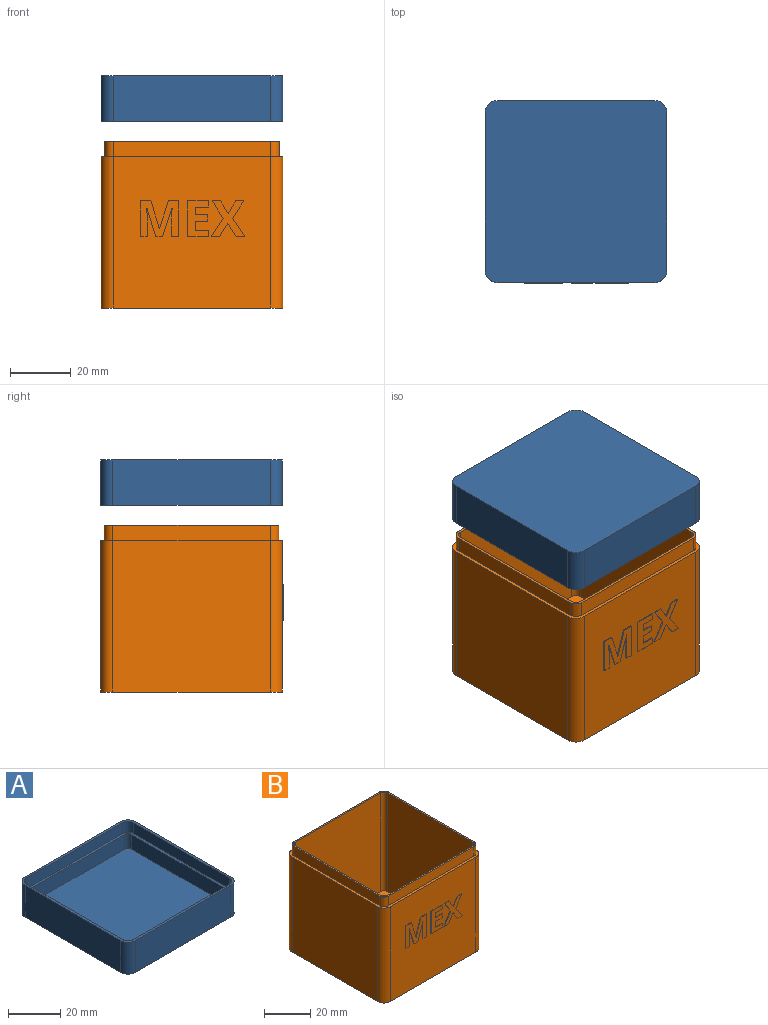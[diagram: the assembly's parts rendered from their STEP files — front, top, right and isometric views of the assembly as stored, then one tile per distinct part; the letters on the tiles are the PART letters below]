
ASSEMBLY  parts=2 mates=2
PART A: 28 faces, bbox 60x60x15 mm
  f0: plane 58x58mm, normal (0,0,1), area 223.7mm2, adj f11,f12,f13,f14,f15,f16,f17,f18
  f1: plane 60x60mm, normal (0,0,1), area 230mm2, adj f2,f3,f4,f5,f6,f7,f8,f9
  f2: plane 52x15mm, normal (0,1,0), area 780mm2, adj f1,f3,f9,f10
  f3: cylinder r=4mm len=15mm, axis (0,0,1), area 94.2mm2, adj f1,f2,f4,f10
  f4: plane 52x15mm, normal (-1,0,0), area 780mm2, adj f1,f3,f5,f10
  f5: cylinder r=4mm len=15mm, axis (0,0,1), area 94.2mm2, adj f1,f4,f6,f10
  f6: plane 52x15mm, normal (0,-1,0), area 780mm2, adj f1,f5,f7,f10
  f7: cylinder r=4mm len=15mm, axis (0,0,1), area 94.2mm2, adj f1,f6,f8,f10
  f8: plane 52x15mm, normal (1,0,0), area 780mm2, adj f1,f7,f9,f10
  f9: cylinder r=4mm len=15mm, axis (0,0,1), area 94.2mm2, adj f1,f2,f8,f10
  f10: plane 60x60mm, normal (0,0,-1), area 3586.3mm2, adj f2,f3,f4,f5,f6,f7,f8,f9
  f11: plane 52x5.1mm, normal (0,-1,0), area 265.2mm2, adj f0,f1,f12,f18
  f12: cylinder r=3mm len=5.1mm, axis (0,0,1), area 24mm2, adj f0,f1,f11,f13
  f13: plane 52x5.1mm, normal (1,0,0), area 265.2mm2, adj f0,f1,f12,f14
  f14: cylinder r=3mm len=5.1mm, axis (0,0,1), area 24mm2, adj f0,f1,f13,f15
  f15: plane 52x5.1mm, normal (0,1,0), area 265.2mm2, adj f0,f1,f14,f16
  f16: cylinder r=3mm len=5.1mm, axis (0,0,1), area 24mm2, adj f0,f1,f15,f17
  f17: plane 52x5.1mm, normal (-1,0,0), area 265.2mm2, adj f0,f1,f16,f18
  f18: cylinder r=3mm len=5.1mm, axis (0,0,1), area 24mm2, adj f0,f1,f11,f17
  f19: plane 52x6.9mm, normal (0,-1,0), area 358.8mm2, adj f0,f20,f26,f27
  f20: cylinder r=2mm len=6.9mm, axis (0,0,-1), area 21.7mm2, adj f0,f19,f21,f27
  f21: plane 52x6.9mm, normal (1,0,0), area 358.8mm2, adj f0,f20,f22,f27
  f22: cylinder r=2mm len=6.9mm, axis (0,0,-1), area 21.7mm2, adj f0,f21,f23,f27
  f23: plane 52x6.9mm, normal (0,1,0), area 358.8mm2, adj f0,f22,f24,f27
  f24: cylinder r=2mm len=6.9mm, axis (0,0,-1), area 21.7mm2, adj f0,f23,f25,f27
  f25: plane 52x6.9mm, normal (-1,0,0), area 358.8mm2, adj f0,f24,f26,f27
  f26: cylinder r=2mm len=6.9mm, axis (0,0,-1), area 21.7mm2, adj f0,f19,f25,f27
  f27: plane 56x56mm, normal (0,0,1), area 3132.6mm2, adj f19,f20,f21,f22,f23,f24,f25,f26
PART B: 74 faces, bbox 60x60.3x55 mm
  f0: plane 52x50mm, normal (0,-1,0), area 2389.2mm2, adj f2,f8,f9,f10,f28,f29,f30,f31
  f1: plane 57.6x57.6mm, normal (0,0,1), area 178.5mm2, adj f11,f12,f13,f14,f15,f16,f17,f18
  f2: plane 60x60mm, normal (0,0,1), area 275.2mm2, adj f0,f3,f4,f5,f6,f7,f8,f9
  f3: plane 52x50mm, normal (1,0,0), area 2600mm2, adj f2,f4,f9,f10
  f4: cylinder r=4mm len=50mm, axis (0,0,1), area 314.2mm2, adj f2,f3,f5,f10
  f5: plane 52x50mm, normal (0,1,0), area 2600mm2, adj f2,f4,f6,f10
  f6: cylinder r=4mm len=50mm, axis (0,0,1), area 314.2mm2, adj f2,f5,f7,f10
  f7: plane 52x50mm, normal (-1,0,0), area 2600mm2, adj f2,f6,f8,f10
  f8: cylinder r=4mm len=50mm, axis (0,0,1), area 314.2mm2, adj f0,f2,f7,f10
  f9: cylinder r=4mm len=50mm, axis (0,0,1), area 314.2mm2, adj f0,f2,f3,f10
  f10: plane 60x60mm, normal (0,0,-1), area 3586.3mm2, adj f0,f3,f4,f5,f6,f7,f8,f9
  f11: plane 52x5mm, normal (1,0,0), area 260mm2, adj f1,f2,f12,f18
  f12: cylinder r=2.8mm len=5mm, axis (0,0,1), area 22mm2, adj f1,f2,f11,f13
  f13: plane 52x5mm, normal (0,1,0), area 260mm2, adj f1,f2,f12,f14
  f14: cylinder r=2.8mm len=5mm, axis (0,0,1), area 22mm2, adj f1,f2,f13,f15
  f15: plane 52x5mm, normal (-1,0,0), area 260mm2, adj f1,f2,f14,f16
  f16: cylinder r=2.8mm len=5mm, axis (0,0,1), area 22mm2, adj f1,f2,f15,f17
  f17: plane 52x5mm, normal (0,-1,0), area 260mm2, adj f1,f2,f16,f18
  f18: cylinder r=2.8mm len=5mm, axis (0,0,1), area 22mm2, adj f1,f2,f11,f17
  f19: plane 52x52mm, normal (-1,0,0), area 2704mm2, adj f1,f20,f26,f27
  f20: cylinder r=2mm len=52mm, axis (0,0,1), area 163.4mm2, adj f1,f19,f21,f27
  f21: plane 52x52mm, normal (0,-1,0), area 2704mm2, adj f1,f20,f22,f27
  f22: cylinder r=2mm len=52mm, axis (0,0,1), area 163.4mm2, adj f1,f21,f23,f27
  f23: plane 52x52mm, normal (1,0,0), area 2704mm2, adj f1,f22,f24,f27
  f24: cylinder r=2mm len=52mm, axis (0,0,1), area 163.4mm2, adj f1,f23,f25,f27
  f25: plane 52x52mm, normal (0,1,0), area 2704mm2, adj f1,f24,f26,f27
  f26: cylinder r=2mm len=52mm, axis (0,0,1), area 163.4mm2, adj f1,f19,f25,f27
  f27: plane 56x56mm, normal (0,0,1), area 3132.6mm2, adj f19,f20,f21,f22,f23,f24,f25,f26
  f28: plane 9.25x3.05mm, normal (0.95,0,-0.31), area 2.9mm2, adj f0,f29,f46,f47
  f29: plane 0.3x0.07mm, normal (0,0,-1), area 0mm2, adj f0,f28,f30,f47
  f30: extruded ~2.75x0.3mm, area 0.8mm2, adj f0,f29,f31,f47
  f31: extruded ~0.91x0.3mm, area 0.3mm2, adj f0,f30,f32,f47
  f32: plane 5.59x0.3mm, normal (-1,0,0), area 1.7mm2, adj f0,f31,f33,f47
  f33: plane 2.33x0.3mm, normal (0,0,-1), area 0.7mm2, adj f0,f32,f34,f47
  f34: plane 11.81x0.3mm, normal (1,0,0), area 3.5mm2, adj f0,f33,f35,f47
  f35: plane 3.41x0.3mm, normal (0,0,1), area 1mm2, adj f0,f34,f36,f47
  f36: plane 9.03x2.97mm, normal (-0.95,0,0.31), area 2.9mm2, adj f0,f35,f37,f47
  f37: plane 0.3x0.05mm, normal (0,0,1), area 0mm2, adj f0,f36,f38,f47
  f38: plane 9.03x2.79mm, normal (0.96,0,0.3), area 2.8mm2, adj f0,f37,f39,f47
  f39: plane 3.41x0.3mm, normal (0,0,1), area 1mm2, adj f0,f38,f40,f47
  f40: plane 11.81x0.3mm, normal (-1,0,0), area 3.5mm2, adj f0,f39,f41,f47
  f41: plane 2.24x0.3mm, normal (0,0,-1), area 0.7mm2, adj f0,f40,f42,f47
  f42: plane 5.49x0.3mm, normal (1,0,0), area 1.6mm2, adj f0,f41,f43,f47
  f43: extruded ~3.77x0.3mm, area 1.1mm2, adj f0,f42,f44,f47
  f44: plane 0.3x0.07mm, normal (0,0,-1), area 0mm2, adj f0,f43,f45,f47
  f45: plane 9.26x2.84mm, normal (-0.96,0,-0.29), area 2.9mm2, adj f0,f44,f46,f47
  f46: plane 2.3x0.3mm, normal (0,0,-1), area 0.7mm2, adj f0,f28,f45,f47
  f47: plane 12.62x11.81mm, normal (0,-1,0), area 96.2mm2, adj f28,f29,f30,f31,f32,f33,f34,f35
  f48: plane 4.3x0.3mm, normal (0,0,1), area 1.3mm2, adj f0,f49,f59,f60
  f49: plane 3.05x0.3mm, normal (1,0,0), area 0.9mm2, adj f0,f48,f50,f60
  f50: plane 4x0.3mm, normal (0,0,-1), area 1.2mm2, adj f0,f49,f51,f60
  f51: plane 2.05x0.3mm, normal (1,0,0), area 0.6mm2, adj f0,f50,f52,f60
  f52: plane 4x0.3mm, normal (0,0,1), area 1.2mm2, adj f0,f51,f53,f60
  f53: plane 2.59x0.3mm, normal (1,0,0), area 0.8mm2, adj f0,f52,f54,f60
  f54: plane 4.3x0.3mm, normal (0,0,-1), area 1.3mm2, adj f0,f53,f55,f60
  f55: plane 2.05x0.3mm, normal (1,0,0), area 0.6mm2, adj f0,f54,f56,f60
  f56: plane 6.8x0.3mm, normal (0,0,1), area 2mm2, adj f0,f55,f57,f60
  f57: plane 11.81x0.3mm, normal (-1,0,0), area 3.5mm2, adj f0,f56,f58,f60
  f58: plane 6.8x0.3mm, normal (0,0,-1), area 2mm2, adj f0,f57,f59,f60
  f59: plane 2.07x0.3mm, normal (1,0,0), area 0.6mm2, adj f0,f48,f58,f60
  f60: plane 11.81x6.8mm, normal (0,-1,0), area 55.5mm2, adj f48,f49,f50,f51,f52,f53,f54,f55
  f61: plane 5.86x3.71mm, normal (0.85,0,-0.53), area 2.1mm2, adj f0,f62,f72,f73
  f62: plane 2.7x0.3mm, normal (0,0,1), area 0.8mm2, adj f0,f61,f63,f73
  f63: plane 4.25x2.5mm, normal (-0.86,0,0.51), area 1.5mm2, adj f0,f62,f64,f73
  f64: plane 4.25x2.54mm, normal (0.86,0,0.51), area 1.5mm2, adj f0,f63,f65,f73
  f65: plane 2.76x0.3mm, normal (0,0,1), area 0.8mm2, adj f0,f64,f66,f73
  f66: plane 5.72x3.67mm, normal (-0.84,0,-0.54), area 2mm2, adj f0,f65,f67,f73
  f67: plane 6.09x3.92mm, normal (-0.84,0,0.54), area 2.2mm2, adj f0,f66,f68,f73
  f68: plane 2.68x0.3mm, normal (0,0,-1), area 0.8mm2, adj f0,f67,f69,f73
  f69: plane 4.47x2.75mm, normal (0.85,0,-0.52), area 1.6mm2, adj f0,f68,f70,f73
  f70: plane 4.47x2.75mm, normal (-0.85,0,-0.52), area 1.6mm2, adj f0,f69,f71,f73
  f71: plane 2.86x0.3mm, normal (0,0,-1), area 0.9mm2, adj f0,f70,f72,f73
  f72: plane 5.95x3.99mm, normal (0.83,0,0.56), area 2.2mm2, adj f0,f61,f71,f73
  f73: plane 11.81x11.04mm, normal (0,-1,0), area 59.1mm2, adj f61,f62,f63,f64,f65,f66,f67,f68
PLACE A rot(axis=(0,1,0),180deg) t=(1.08,-0.17,77.09)mm
PLACE B t=(1.08,-0.17,0.49)mm
MATE slider A.f10 <-> B.f10  axis (0,0,1) through (1.08,-0.17,77.09)mm
MATE parallel B.f10 <-> A.f10  axis (0,0,-1) through (1.08,-0.17,0.49)mm
